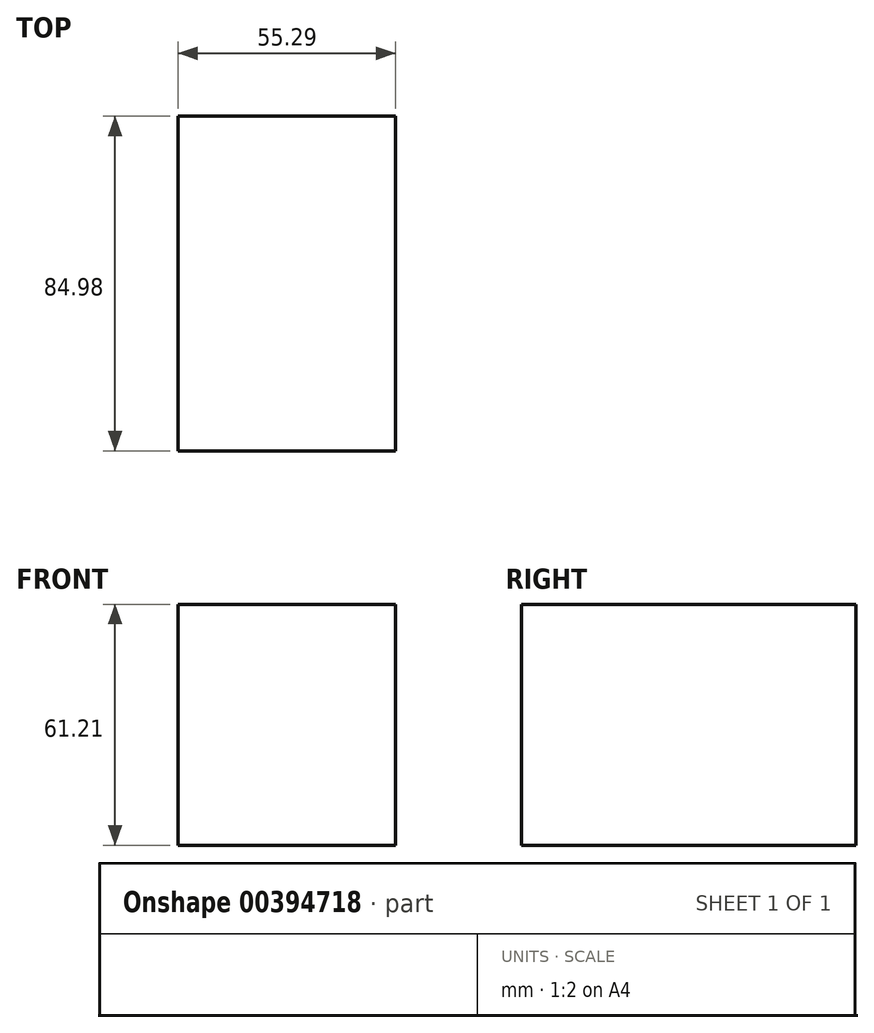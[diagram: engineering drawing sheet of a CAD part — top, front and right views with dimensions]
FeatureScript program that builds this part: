
annotation { "Feature Type Name" : "Feature", "Feature Type Description" : "" }
export const myFeature = defineFeature(function(context is Context, id is Id, definition is map)
    precondition{}
    {
        {
            var Q0;
            Q0=qCreatedBy(makeId("Top.planeOp"),FACE);
            var sketch = newSketch(context, id + "F0", { "sketchPlane" : qUnion([Q0])});
            skLineSegment(sketch, "E0.bottom", {"start": v(-6.1, -30.38) * mm, "end": v(-61.4, -30.38) * mm});
            skLineSegment(sketch, "E0.top", {"start": v(-6.1, 54.6) * mm, "end": v(-61.4, 54.6) * mm});
            skLineSegment(sketch, "E0.left", {"start": v(-6.1, -30.38) * mm, "end": v(-6.1, 54.6) * mm});
            skLineSegment(sketch, "E0.right", {"start": v(-61.4, -30.38) * mm, "end": v(-61.4, 54.6) * mm});
            skSolve(sketch);
        }
        {
            var Q0;
            Q0 = qSketchRegion(id + "F0", true);
            extrude(context, id + "F1", {"entities" : qUnion([Q0]), "depth" : 61.2 * mm});
        }
    });
